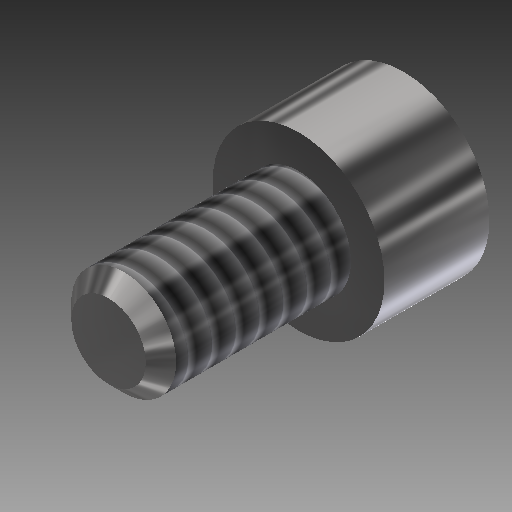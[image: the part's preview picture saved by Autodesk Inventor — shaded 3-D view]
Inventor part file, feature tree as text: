
AUTODESK INVENTOR PART (.ipt)
format: ipt  version: 2017 (Build 210142000, 142)  size: 186,368 bytes
history: native  units: in
note: dims shown in document units (in); Inventor stores cm internally (conversion verified against a paired STEP export)
features: extrude x3, sketch x3, thread x1, chamfer x1
ambient origin geometry x8: Origin, YZ Plane, XZ Plane, XY Plane, X Axis, Y Axis, Z Axis, Center Point
bodies: Solid1 (feature_tree)
feature tree (8):
  extrude  "Extrusion1"  Depth=0.25in TaperAngle=0.0deg
  extrude  "Extrusion2"  Depth=0.138in TaperAngle=0.0deg
  extrude  "Extrusion3"  Depth=0.069in TaperAngle=0.0deg
  thread  "Thread1"  [1 undecoded]
  chamfer  "Chamfer1"  Distance=0.02in Angle=45.0deg
  sketch  "Sketch1"  dims[d0=0.138in d1=0.25in d2=0.0in]
  sketch  "Sketch2"  dims[d3=0.226in d4=0.138in d5=0.0in]
  sketch  "Sketch3"  dims[d6=0.1094in d7=0.069in d8=0.0in d9=1.0in d10=0.0in d11=0.02in d12=0.125in d13=45.0deg]
note: 1 required parameter value undecoded (feature->parameter linkage not recoverable at this tier; creation-order binding heuristic only, values carry confidence <= 0.55)
